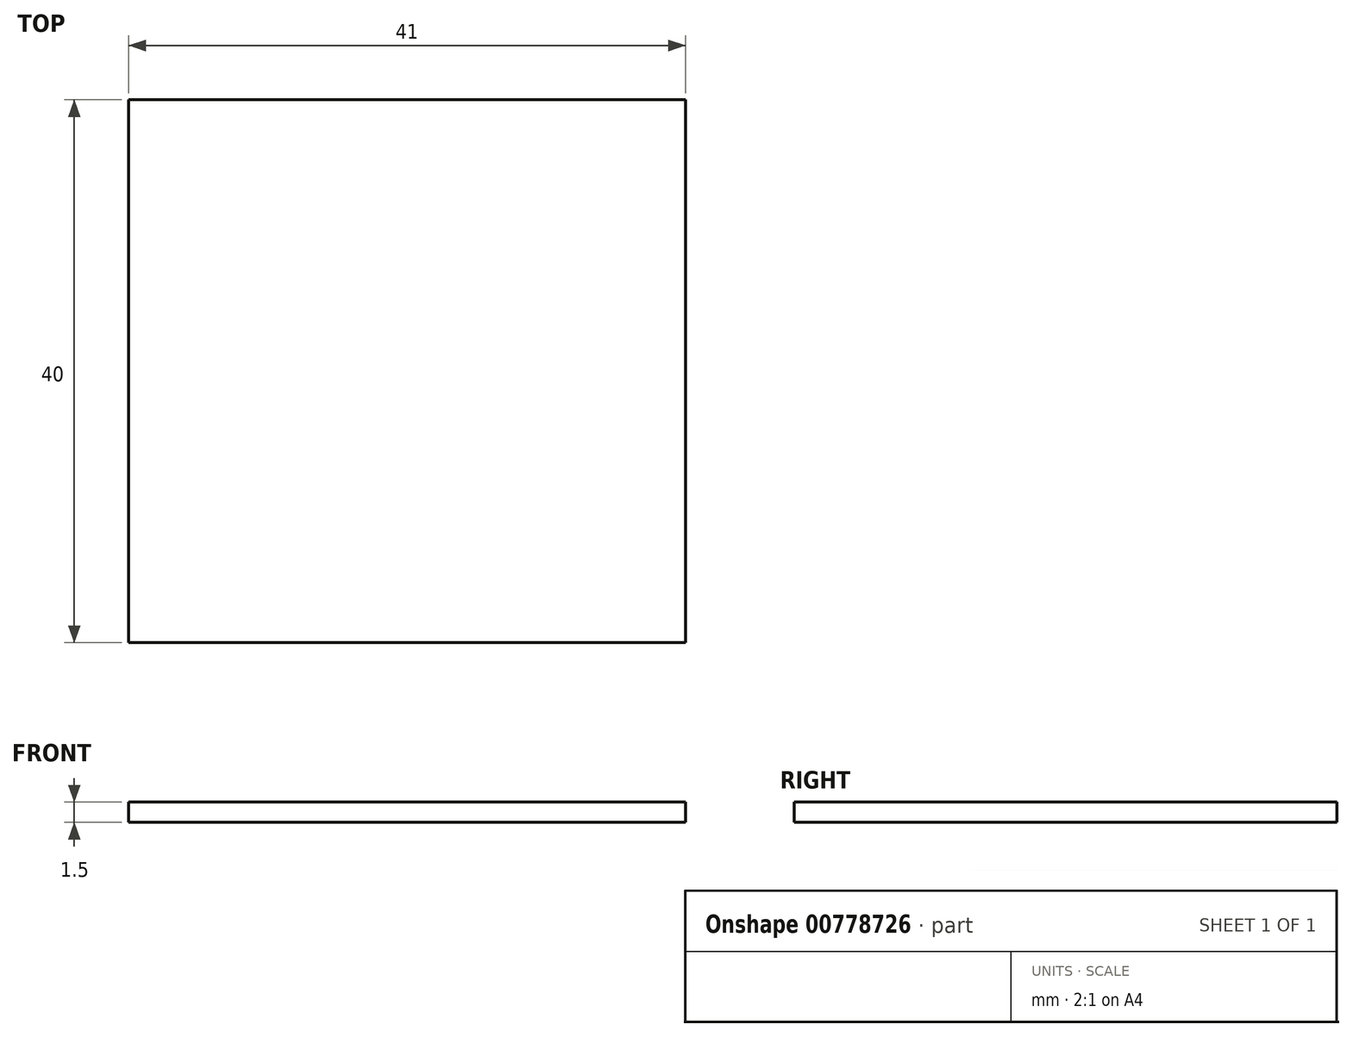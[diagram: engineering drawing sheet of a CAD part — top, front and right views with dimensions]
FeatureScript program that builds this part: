
annotation { "Feature Type Name" : "Feature", "Feature Type Description" : "" }
export const myFeature = defineFeature(function(context is Context, id is Id, definition is map)
    precondition{}
    {
        {
            var Q0;
            Q0=qCreatedBy(makeId("Top.planeOp"),FACE);
            var sketch = newSketch(context, id + "F0", { "sketchPlane" : qUnion([Q0])});
            skLineSegment(sketch, "E0.bottom", {"start": v(20.5, -20) * mm, "end": v(-20.5, -20) * mm});
            skLineSegment(sketch, "E0.top", {"start": v(20.5, 20) * mm, "end": v(-20.5, 20) * mm});
            skLineSegment(sketch, "E0.left", {"start": v(20.5, -20) * mm, "end": v(20.5, 20) * mm});
            skLineSegment(sketch, "E0.right", {"start": v(-20.5, -20) * mm, "end": v(-20.5, 20) * mm});
            skPoint(sketch, "E0.middle", {"position": v(0, 0) * mm});
            skSolve(sketch);
        }
        {
            var Q0;
            Q0=makeQuery(id+"F0.imprint","IMPRINT",FACE,{"disambiguationData":[TD([[makeQuery(id+"F0.imprint","IMPRINT",EDGE,{"derivedFrom":sQuery(id+"F0.wireOp",EDGE,"E0.bottom")}),-1.0]])]});
            extrude(context, id + "F1", {"entities" : qUnion([Q0]), "depth" : 1.5 * mm, "offsetDistance" : 25 * mm});
        }
    });
